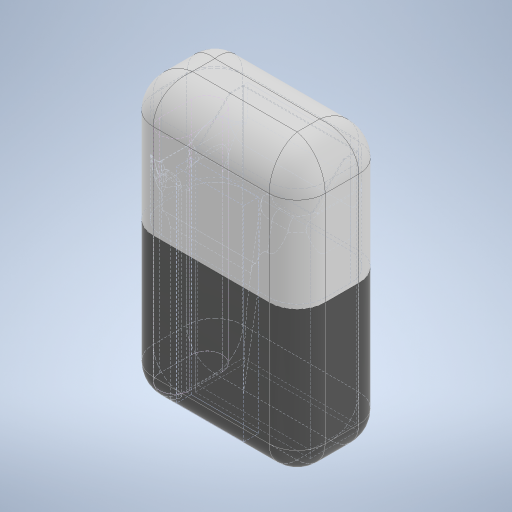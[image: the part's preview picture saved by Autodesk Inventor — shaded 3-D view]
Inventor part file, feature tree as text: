
AUTODESK INVENTOR PART (.ipt)
format: ipt  version: 2023 (Build 270158030, 158C)  size: 1,092,096 bytes
history: native  units: mm
features: fillet x15, sketch x15, extrude x14, other x5, chamfer x1
ambient origin geometry x8: Origin, YZ Plane, XZ Plane, XY Plane, X Axis, Y Axis, Z Axis, Center Point
bodies: Solid7 (feature_tree)
feature tree (50):
  other  "filtercase"
  extrude  "Extrusion1"  Depth=40.97mm
  extrude  "Extrusion2"  Depth=0.32mm
  extrude  "Extrusion3"  Depth=0.32mm
  extrude  "Extrusion4"  Depth=84.0mm TaperAngle=0.0deg
  extrude  "Extrusion5"  Depth=5.0mm
  extrude  "Extrusion6"  Depth=5.1mm
  extrude  "Extrusion7"  Depth=1.5mm
  extrude  "Extrusion8"  Depth=10.0mm TaperAngle=0.0deg
  extrude  "Extrusion9"  Depth=5.3mm
  extrude  "Extrusion10"  Depth=10.75mm
  chamfer  "Chamfer1"  Distance=78.88mm
  fillet  "Fillet2"  Radius=3.0mm
  fillet  "Fillet3"  Radius=3.0mm
  fillet  "Fillet4"  Radius=78.88mm
  fillet  "Fillet5"  Radius=3.0mm
  fillet  "Fillet6"  Radius=1.55mm
  fillet  "Fillet7"  Radius=1.55mm
  fillet  "Fillet8"  Radius=1.55mm
  fillet  "Fillet9"  Radius=1.55mm
  fillet  "Fillet10"  Radius=25.0mm
  fillet  "Fillet11"  Radius=2.0mm
  fillet  "Fillet12"  [1 undecoded]
  fillet  "Fillet13"  Radius=10.0mm
  sketch  "Sketch12"  dims[d25=22.26mm]
  extrude  "Extrusion11"  Depth=10.0mm
  extrude  "Extrusion12"  Depth=10.0mm
  fillet  "Fillet14"  Radius=10.0mm
  sketch  "Sketch15"  dims[d28=-5.815mm]
  fillet  "Fillet15"  Radius=10.0mm
  extrude  "Extrusion13"  Depth=10.0mm
  extrude  "Extrusion14"  Depth=10.0mm
  fillet  "Fillet16"  Radius=13.0mm
  sketch  "Sketch1"  dims[d0=17.1mm d1=40.97mm]
  sketch  "Sketch2"  dims[d2=86.3mm d3=0.0mm d4=0.32mm]
  sketch  "Sketch3"  dims[d5=0.32mm d6=0.32mm]
  sketch  "Sketch4"  dims[d7=0.32mm d8=84.0mm d9=0.0mm]
  other  "roll-buddy-body"
  sketch  "Sketch5"  dims[d10=1.3mm d11=5.0mm]
  other  "rizler"
  sketch  "Sketch7"  dims[d12=0.0mm d13=0.0mm d14=5.1mm]
  other  "cricket"
  sketch  "Sketch8"  dims[d15=1.5mm d16=1.5mm]
  sketch  "Sketch9"  dims[d17=5.1mm d18=10.0mm d19=0.0mm]
  sketch  "Sketch10"  dims[d20=24.0mm d21=5.3mm]
  sketch  "Sketch11"  dims[d22=73.0mm d23=0.0mm d24=10.75mm]
  sketch  "Sketch13"  dims[d26=1.0mm]
  sketch  "Sketch14"  dims[d27=11.19mm]
  other  "lid"
  sketch  "Sketch16"  dims[d29=0.925mm d30=78.88mm d31=0.0mm d32=3.0mm d33=3.0mm d34=78.88mm d35=0.0mm d36=3.0mm d37=0.0mm d38=1.55mm d39=1.55mm d40=1.55mm d41=1.55mm d42=25.0mm d43=0.0mm d44=2.0mm d45=2.0mm d46=13.962634mm d48=0.0mm d49=0.0mm d51=10.0mm d52=8.0mm d53=10.0mm d54=10.0mm d55=10.0mm d56=10.0mm d57=10.0mm d58=13.0mm d59=13.0mm d60=1.0mm d61=1.0mm d62=0.1mm d63=0.1mm d64=1.122mm d65=0.0mm d66=1.122mm d67=0.0mm d68=4.35mm d69=1.5mm d70=1.5mm d71=1.5mm d72=1.5mm d73=3.0mm d74=10.0mm d75=10.0mm d76=0.0mm d77=10.0mm d78=0.0mm d79=12.0mm]
note: 1 required parameter value undecoded (feature->parameter linkage not recoverable at this tier; creation-order binding heuristic only, values carry confidence <= 0.55)
